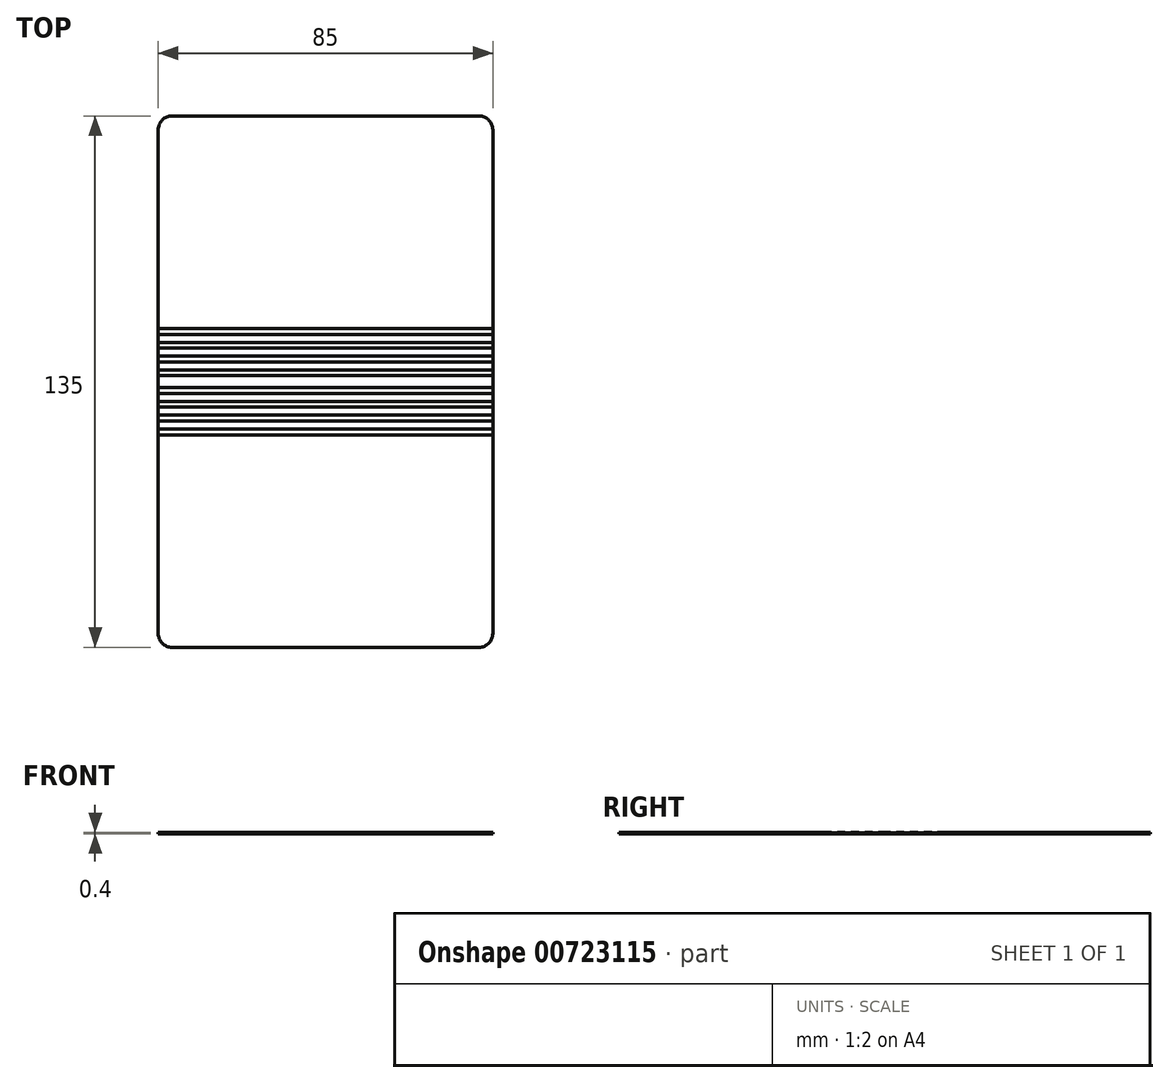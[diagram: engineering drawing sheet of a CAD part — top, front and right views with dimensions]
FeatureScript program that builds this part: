
annotation { "Feature Type Name" : "Feature", "Feature Type Description" : "" }
export const myFeature = defineFeature(function(context is Context, id is Id, definition is map)
    precondition{}
    {
        {
            var Q0;
            Q0=qCreatedBy(makeId("Top.planeOp"),FACE);
            var sketch = newSketch(context, id + "F0", { "sketchPlane" : qUnion([Q0])});
            skLineSegment(sketch, "E0.bottom", {"start": v(39, 67.5) * mm, "end": v(-39, 67.5) * mm});
            skLineSegment(sketch, "E0.top", {"start": v(39, -67.5) * mm, "end": v(-39, -67.5) * mm});
            skLineSegment(sketch, "E0.left", {"start": v(42.5, 64) * mm, "end": v(42.5, -64) * mm});
            skLineSegment(sketch, "E0.right", {"start": v(-42.5, 64) * mm, "end": v(-42.5, -64) * mm});
            skPoint(sketch, "E0.middle", {"position": v(0, 0) * mm});
            skPoint(sketch, "E1.visualSharp", {"position": v(-42.5, 67.5) * mm});
            skArc(sketch, "E1.filletArc", {"start": v(-39, 67.5) * mm, "mid": v(-41.47, 66.47) * mm, "end": v(-42.5, 64) * mm});
            skPoint(sketch, "E2.visualSharp", {"position": v(42.5, 67.5) * mm});
            skArc(sketch, "E2.filletArc", {"start": v(42.5, 64) * mm, "mid": v(41.47, 66.47) * mm, "end": v(39, 67.5) * mm});
            skPoint(sketch, "E3.visualSharp", {"position": v(42.5, -67.5) * mm});
            skArc(sketch, "E3.filletArc", {"start": v(39, -67.5) * mm, "mid": v(41.47, -66.47) * mm, "end": v(42.5, -64) * mm});
            skPoint(sketch, "E4.visualSharp", {"position": v(-42.5, -67.5) * mm});
            skArc(sketch, "E4.filletArc", {"start": v(-42.5, -64) * mm, "mid": v(-41.47, -66.47) * mm, "end": v(-39, -67.5) * mm});
            skSolve(sketch);
        }
        {
            var Q0;
            Q0 = qSketchRegion(id + "F0", true);
            extrude(context, id + "F1", {"entities" : qUnion([Q0]), "depth" : .2 * mm, "offsetDistance" : 25 * mm});
        }
        {
            var Q0;
            Q0=makeQuery(id+"F1.opExtrude","CAP_FACE",FACE,{"disambiguationData":[OSD([sQuery(id+"F0.wireOp",EDGE,"E0.bottom"),sQuery(id+"F0.wireOp",EDGE,"E0.top"),sQuery(id+"F0.wireOp",EDGE,"E0.left"),sQuery(id+"F0.wireOp",EDGE,"E0.right"),sQuery(id+"F0.wireOp",EDGE,"E1.filletArc"),sQuery(id+"F0.wireOp",EDGE,"E2.filletArc"),sQuery(id+"F0.wireOp",EDGE,"E3.filletArc"),sQuery(id+"F0.wireOp",EDGE,"E4.filletArc")])],"isStart":false});
            var sketch = newSketch(context, id + "F2", { "sketchPlane" : qUnion([Q0])});
            skLineSegment(sketch, "E5.bottom", {"start": v(-42.5, 12) * mm, "end": v(42.5, 12) * mm});
            skLineSegment(sketch, "E5.top", {"start": v(-42.5, 13.5) * mm, "end": v(42.5, 13.5) * mm});
            skLineSegment(sketch, "E5.left", {"start": v(-42.5, 12) * mm, "end": v(-42.5, 13.5) * mm});
            skLineSegment(sketch, "E5.right", {"start": v(42.5, 12) * mm, "end": v(42.5, 13.5) * mm});
            skLineSegment(sketch, "E6.0.1.0", {"start": v(-42.5, 8.5) * mm, "end": v(42.5, 8.5) * mm});
            skLineSegment(sketch, "E6.0.1.1", {"start": v(-42.5, 10) * mm, "end": v(42.5, 10) * mm});
            skLineSegment(sketch, "E6.0.1.2", {"start": v(42.5, 8.5) * mm, "end": v(42.5, 10) * mm});
            skLineSegment(sketch, "E6.0.1.3", {"start": v(-42.5, 8.5) * mm, "end": v(-42.5, 10) * mm});
            skLineSegment(sketch, "E6.0.2.0", {"start": v(-42.5, 5) * mm, "end": v(42.5, 5) * mm});
            skLineSegment(sketch, "E6.0.2.1", {"start": v(-42.5, 6.5) * mm, "end": v(42.5, 6.5) * mm});
            skLineSegment(sketch, "E6.0.2.2", {"start": v(42.5, 5) * mm, "end": v(42.5, 6.5) * mm});
            skLineSegment(sketch, "E6.0.2.3", {"start": v(-42.5, 5) * mm, "end": v(-42.5, 6.5) * mm});
            skLineSegment(sketch, "E6.direction1", {"start": v(-42.5, 12) * mm, "end": v(-17.5, 12) * mm, "construction": true});
            skLineSegment(sketch, "E6.direction2", {"start": v(-42.5, 12) * mm, "end": v(-42.5, 8.5) * mm, "construction": true});
            skLineSegment(sketch, "E7.MirrorCS", {"start": v(-42.5, -12) * mm, "end": v(-42.5, -13.5) * mm});
            skLineSegment(sketch, "E8.MirrorCS", {"start": v(-42.5, -8.5) * mm, "end": v(-42.5, -10) * mm});
            skLineSegment(sketch, "E9.MirrorCS", {"start": v(-42.5, -5) * mm, "end": v(-42.5, -6.5) * mm});
            skLineSegment(sketch, "E10.MirrorCS", {"start": v(42.5, -12) * mm, "end": v(42.5, -13.5) * mm});
            skLineSegment(sketch, "E11.MirrorCS", {"start": v(42.5, -8.5) * mm, "end": v(42.5, -10) * mm});
            skLineSegment(sketch, "E12.MirrorCS", {"start": v(42.5, -5) * mm, "end": v(42.5, -6.5) * mm});
            skLineSegment(sketch, "E13.MirrorCS", {"start": v(-42.5, -5) * mm, "end": v(42.5, -5) * mm});
            skLineSegment(sketch, "E14.MirrorCS", {"start": v(-42.5, -6.5) * mm, "end": v(42.5, -6.5) * mm});
            skLineSegment(sketch, "E15.MirrorCS", {"start": v(-42.5, -8.5) * mm, "end": v(42.5, -8.5) * mm});
            skLineSegment(sketch, "E16.MirrorCS", {"start": v(-42.5, -10) * mm, "end": v(42.5, -10) * mm});
            skLineSegment(sketch, "E17.MirrorCS", {"start": v(-42.5, -12) * mm, "end": v(42.5, -12) * mm});
            skLineSegment(sketch, "E18.MirrorCS", {"start": v(-42.5, -13.5) * mm, "end": v(42.5, -13.5) * mm});
            skLineSegment(sketch, "E19.0.0.3", {"start": v(-42.5, 1.5) * mm, "end": v(42.5, 1.5) * mm});
            skLineSegment(sketch, "E19.3.0.3", {"start": v(-42.5, 3) * mm, "end": v(42.5, 3) * mm});
            skLineSegment(sketch, "E19.6.0.3", {"start": v(42.5, 1.5) * mm, "end": v(42.5, 3) * mm});
            skLineSegment(sketch, "E19.9.0.3", {"start": v(-42.5, 1.5) * mm, "end": v(-42.5, 3) * mm});
            skLineSegment(sketch, "E20.MirrorCS", {"start": v(-42.5, -1.5) * mm, "end": v(-42.5, -3) * mm});
            skLineSegment(sketch, "E21.MirrorCS", {"start": v(42.5, -1.5) * mm, "end": v(42.5, -3) * mm});
            skLineSegment(sketch, "E22.MirrorCS", {"start": v(-42.5, -3) * mm, "end": v(42.5, -3) * mm});
            skLineSegment(sketch, "E23.MirrorCS", {"start": v(-42.5, -1.5) * mm, "end": v(42.5, -1.5) * mm});
            skSolve(sketch);
        }
        {
            var Q0;
            Q0 = qSketchRegion(id + "F0", true);
            extrude(context, id + "F3", {"entities" : qUnion([Q0]), "operationType" : NewBodyOperationType.ADD, "depth" : .4 * mm, "offsetDistance" : 25 * mm});
        }
        {
            var Q0;
            Q0 = qSketchRegion(id + "F2", true);
            var Q1;
            Q1=makeQuery(id+"F3.opExtrude","CAP_FACE",FACE,{"disambiguationData":[OSD([sQuery(id+"F0.wireOp",EDGE,"E0.bottom"),sQuery(id+"F0.wireOp",EDGE,"E0.top"),sQuery(id+"F0.wireOp",EDGE,"E0.left"),sQuery(id+"F0.wireOp",EDGE,"E0.right"),sQuery(id+"F0.wireOp",EDGE,"E1.filletArc"),sQuery(id+"F0.wireOp",EDGE,"E2.filletArc"),sQuery(id+"F0.wireOp",EDGE,"E3.filletArc"),sQuery(id+"F0.wireOp",EDGE,"E4.filletArc")])],"isStart":false});
            extrude(context, id + "F4", {"entities" : qUnion([Q0]), "operationType" : NewBodyOperationType.REMOVE, "endBound" : BoundingType.UP_TO_SURFACE, "depth" : 25 * mm, "endBoundEntityFace" : qUnion([Q1]), "offsetDistance" : 25 * mm});
        }
    });
